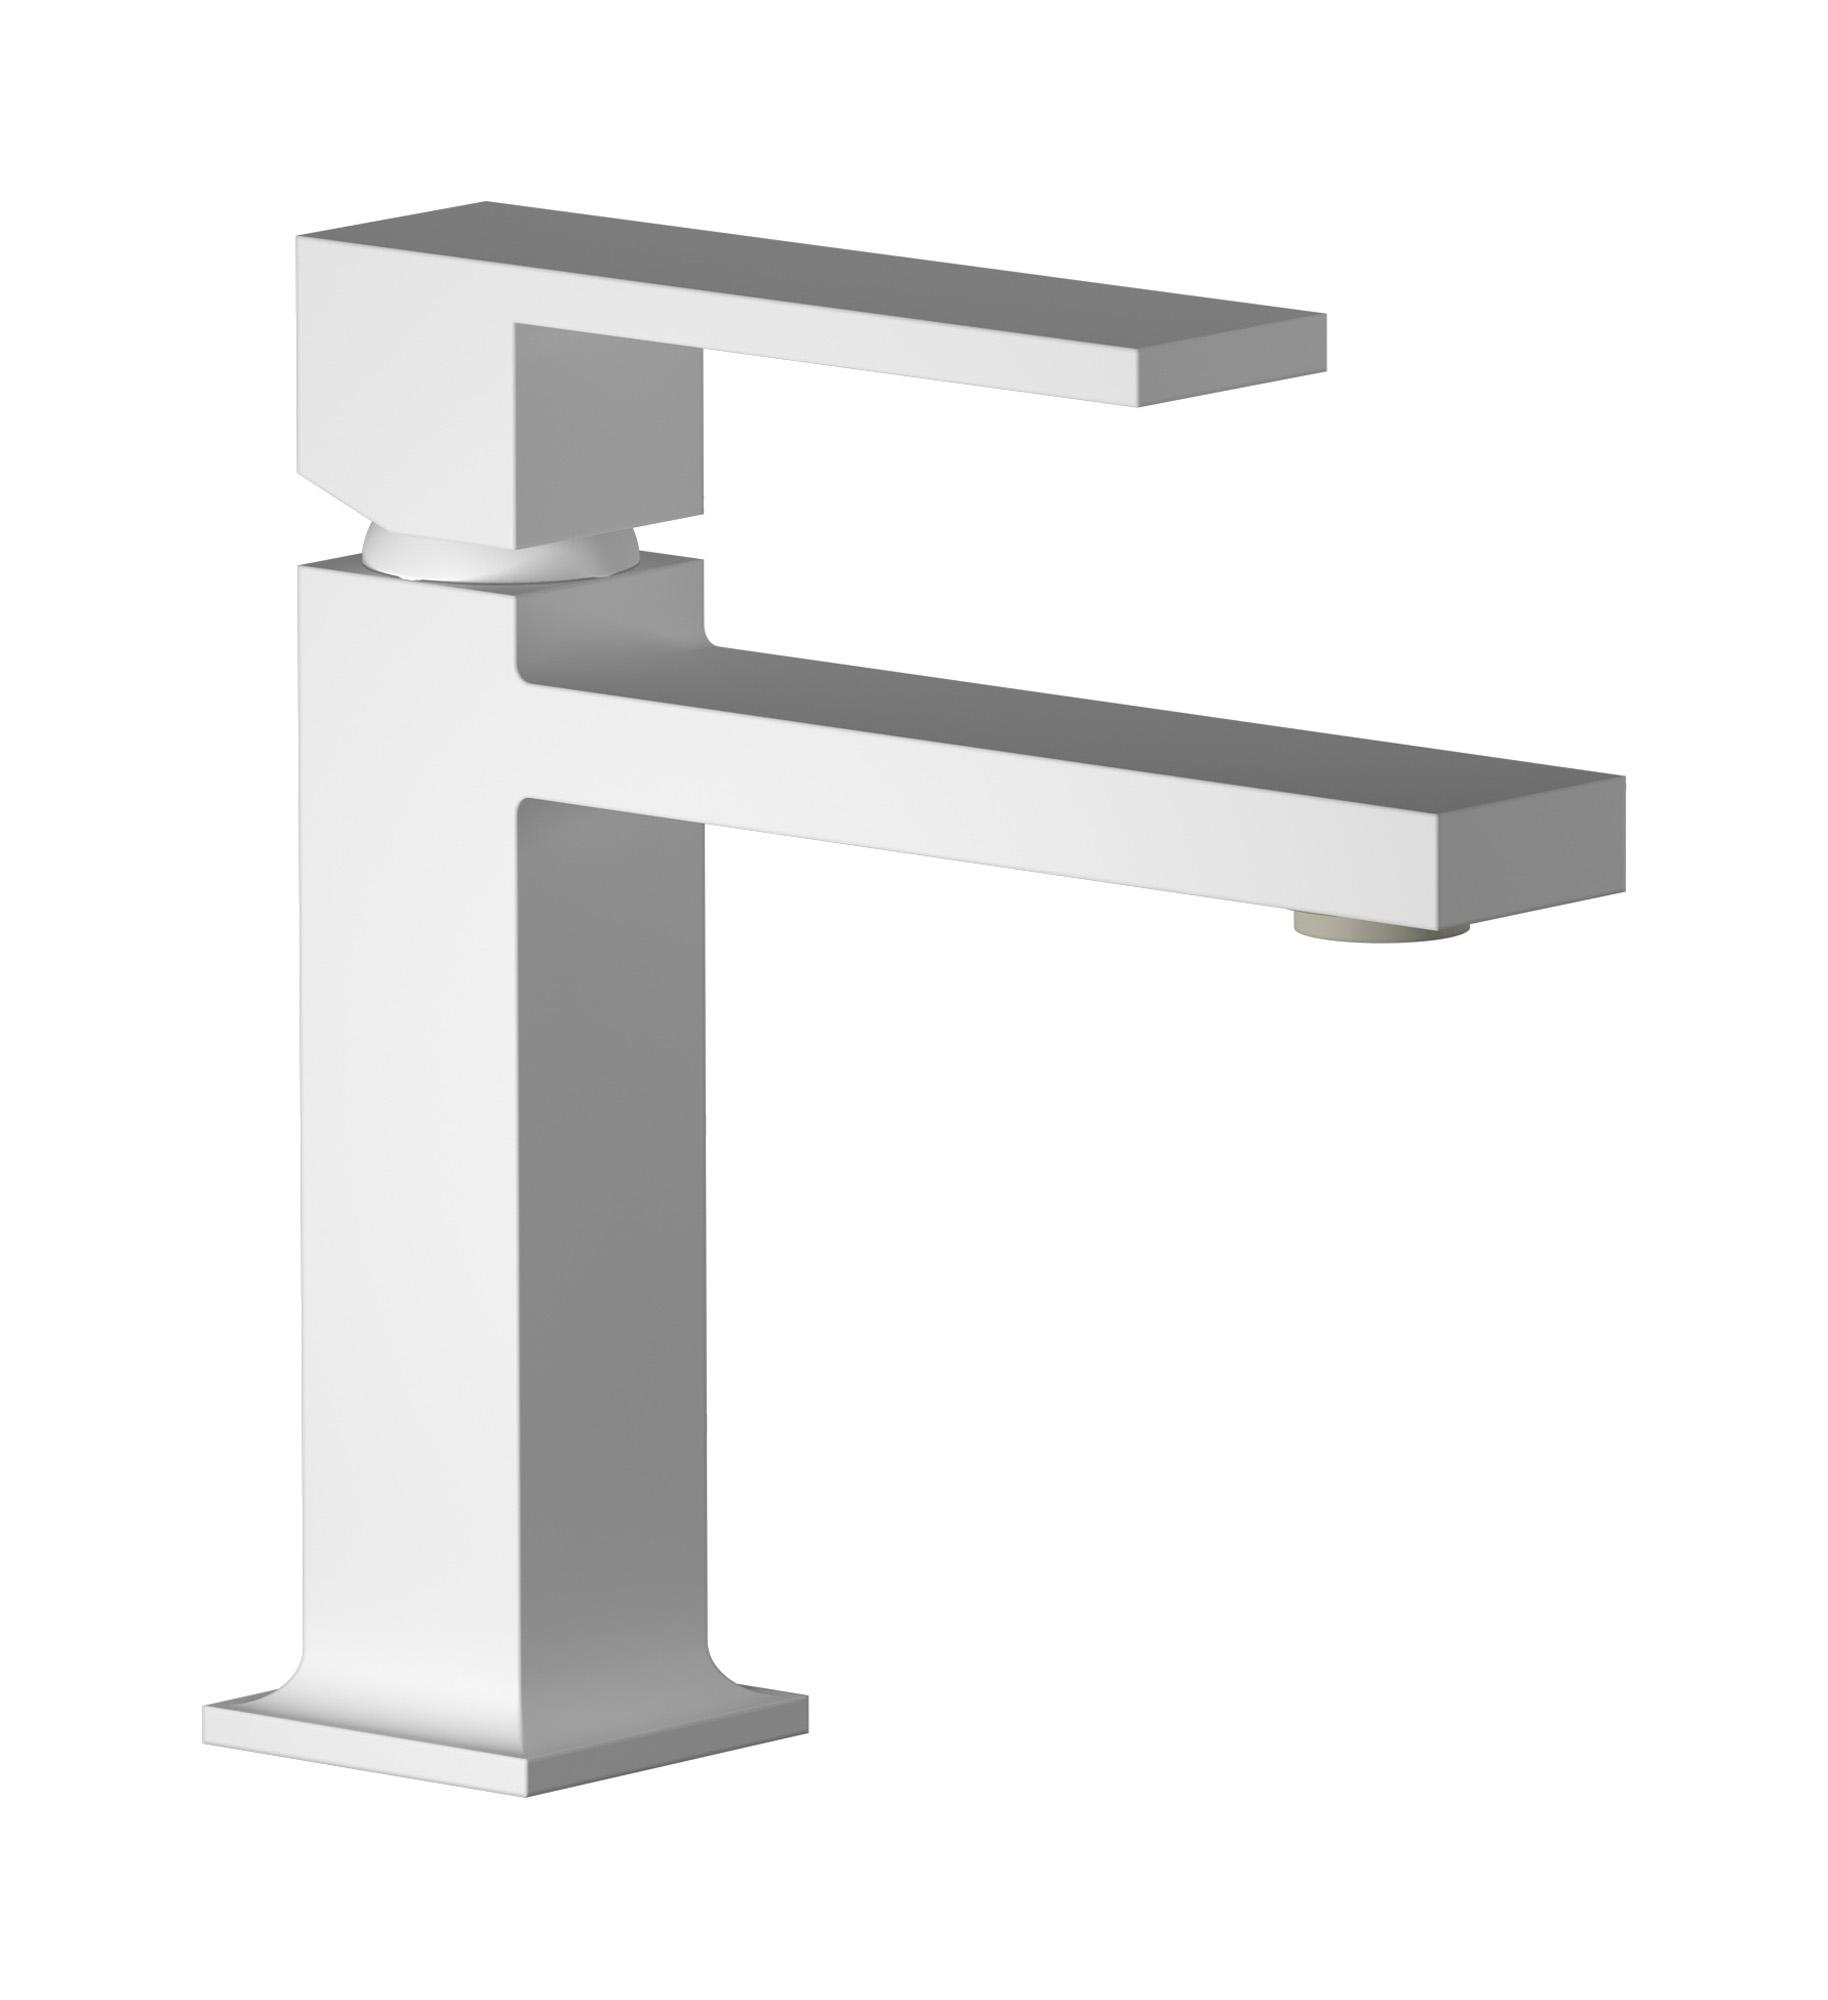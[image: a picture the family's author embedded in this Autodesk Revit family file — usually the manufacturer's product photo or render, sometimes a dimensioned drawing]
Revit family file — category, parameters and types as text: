
# Revit family: RU201
name_source: partatom
category: Apparecchi idraulici
units: mm (PartAtom-declared; Revit-internal decimal feet)

## family parameters
Basato su piano di lavoro = No
Condiviso = No
Mantieni orientamento annotazione = No
Numero OmniClass = 23.45.55.17
Punto di calcolo locali = No
Quota connettore circolare = Usa diametro
Sempre verticale = Sì
Taglio con vuoti quando caricato = No
Tipo di parte = Normale
Titolo OmniClass = Mixing Faucets

## types (12) — shared parameters
Cold water inlet = 10 mm  [stored 0.0328084 ft]
Commenti sul tipo = Mini monohole washbasin mixer complete with drain
Connessione CW = No
Connessione HW = No
Connessione di scarico = No
Connessione di ventilazione = No
Descrizione = Mini monohole washbasin mixer complete with drain
Hot water inlet = 10 mm  [stored 0.0328084 ft]
Produttore = IB Rubinetterie S.p.A.
URL = https://www.weareib.it
zero-valued in all types: Prospetto di default

## per-type parameters (varying)
| type | Finishes surface | Immagine tipo | Modello |
| Chrome | IB_Chrome | RU201CC.jpg | RU201CC |
| Matt White | IB_matt white | RU201BO.jpg | RU201BO |
| Black Chrome | IB_Black chrome | RU201CF.jpg | RU201CF |
| Brushed Black Chrome | IB_Brushed black chrome | RU201CS.jpg | RU201CS |
| Pale Gold | IB_Pale gold | RU201II.jpg | RU201II |
| Brushed Pale Gold | IB_brushed pale gold | RU201IS.jpg | RU201IS |
| Matt Black | IB_matt black | RU201NP.jpg | RU201NP |
| Gold | IB_gold | RU201OO.jpg | RU201OO |
| Brushed Gold | IB_brushed gold | RU201OS.jpg | RU201OS |
| Rose Gold | IB_Rose gold | RU201RS.jpg | RU201RS |
| Brushed Rose Gold | IB_Brushed rose gold | RU201SR.jpg | RU201SR |
| Brushed Nickel | IB_Brushed nickel | RU201SS.jpg | RU201SS |

note: [stored X ft] marks values corroborated as IEEE doubles in the binary element streams (Revit-internal decimal feet)
